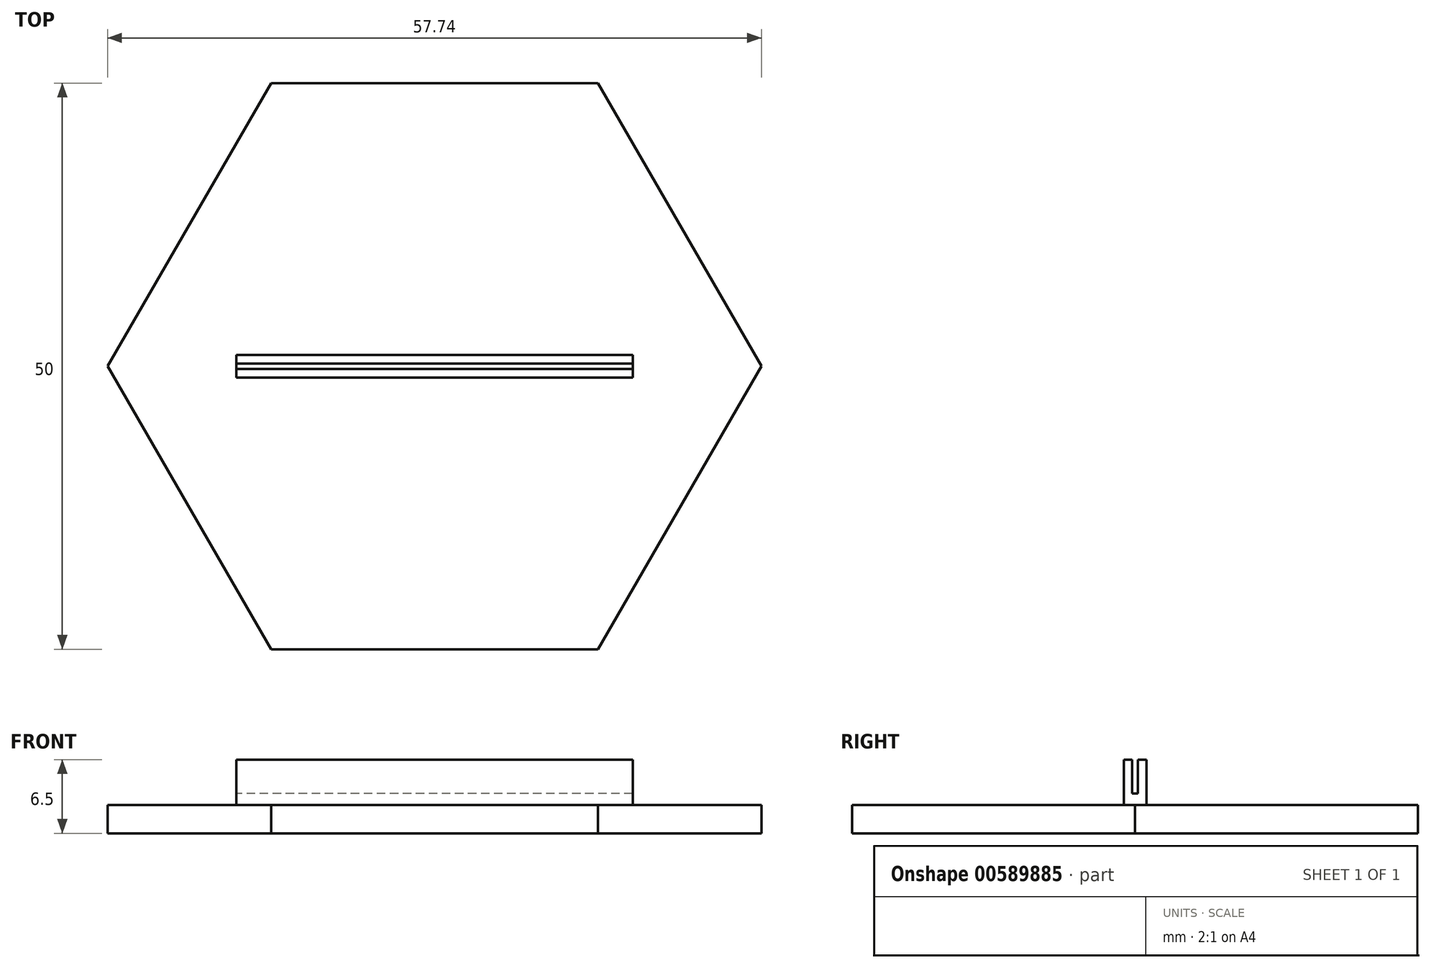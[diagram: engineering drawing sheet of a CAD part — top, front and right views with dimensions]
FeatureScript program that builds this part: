
annotation { "Feature Type Name" : "Feature", "Feature Type Description" : "" }
export const myFeature = defineFeature(function(context is Context, id is Id, definition is map)
    precondition{}
    {
        {
            var Q0;
            Q0=qCreatedBy(makeId("Top.planeOp"),FACE);
            var sketch = newSketch(context, id + "F0", { "sketchPlane" : qUnion([Q0])});
            skCircle(sketch, "E0.cCircle", {"center": v(0, 0) * mm, "radius": 25 * mm, "construction": true});
            skLineSegment(sketch, "E0.0", {"start": v(14.43, -25) * mm, "end": v(-14.43, -25) * mm});
            skLineSegment(sketch, "E0.1", {"start": v(-14.43, -25) * mm, "end": v(-28.87, 0) * mm});
            skLineSegment(sketch, "E0.2", {"start": v(-28.87, 0) * mm, "end": v(-14.43, 25) * mm});
            skLineSegment(sketch, "E0.3", {"start": v(-14.43, 25) * mm, "end": v(14.43, 25) * mm});
            skLineSegment(sketch, "E0.4", {"start": v(14.43, 25) * mm, "end": v(28.87, 0) * mm});
            skLineSegment(sketch, "E0.5", {"start": v(28.87, 0) * mm, "end": v(14.43, -25) * mm});
            skPoint(sketch, "E0.0.midPoint", {"position": v(0, -25) * mm});
            skSolve(sketch);
        }
        {
            var Q0;
            Q0 = qSketchRegion(id + "F0", true);
            extrude(context, id + "F1", {"entities" : qUnion([Q0]), "depth" : 2.5 * mm, "offsetDistance" : 25 * mm});
        }
        {
            var Q0;
            Q0=makeQuery(id+"F1.opExtrude","CAP_FACE",FACE,{"disambiguationData":[OSD([sQuery(id+"F0.wireOp",EDGE,"E0.0"),sQuery(id+"F0.wireOp",EDGE,"E0.1"),sQuery(id+"F0.wireOp",EDGE,"E0.2"),sQuery(id+"F0.wireOp",EDGE,"E0.3"),sQuery(id+"F0.wireOp",EDGE,"E0.4"),sQuery(id+"F0.wireOp",EDGE,"E0.5")])],"isStart":false});
            var sketch = newSketch(context, id + "F2", { "sketchPlane" : qUnion([Q0])});
            skLineSegment(sketch, "E1.bottom", {"start": v(17.5, -1) * mm, "end": v(-17.5, -1) * mm});
            skLineSegment(sketch, "E1.top", {"start": v(17.5, 1) * mm, "end": v(-17.5, 1) * mm});
            skLineSegment(sketch, "E1.left", {"start": v(17.5, -1) * mm, "end": v(17.5, 1) * mm});
            skLineSegment(sketch, "E1.right", {"start": v(-17.5, -1) * mm, "end": v(-17.5, 1) * mm});
            skPoint(sketch, "E1.middle", {"position": v(0, 0) * mm});
            skSolve(sketch);
        }
        {
            var Q0;
            Q0=makeQuery(id+"F2.imprint","IMPRINT",FACE,{"disambiguationData":[TD([[makeQuery(id+"F2.imprint","IMPRINT",EDGE,{"derivedFrom":sQuery(id+"F2.wireOp",EDGE,"E1.bottom")}),-1.0]])]});
            extrude(context, id + "F3", {"entities" : qUnion([Q0]), "operationType" : NewBodyOperationType.ADD, "depth" : 4 * mm, "offsetDistance" : 25 * mm});
        }
        {
            var Q0;
            Q0=makeQuery(id+"F3.opExtrude","CAP_FACE",FACE,{"disambiguationData":[OSD([sQuery(id+"F2.wireOp",EDGE,"E1.bottom"),sQuery(id+"F2.wireOp",EDGE,"E1.top"),sQuery(id+"F2.wireOp",EDGE,"E1.left"),sQuery(id+"F2.wireOp",EDGE,"E1.right")])],"isStart":false});
            var sketch = newSketch(context, id + "F4", { "sketchPlane" : qUnion([Q0])});
            skLineSegment(sketch, "E2.bottom", {"start": v(25.28, -0.25) * mm, "end": v(-24.72, -0.25) * mm});
            skLineSegment(sketch, "E2.top", {"start": v(25.28, 0.25) * mm, "end": v(-24.72, 0.25) * mm});
            skLineSegment(sketch, "E2.left", {"start": v(25.28, -0.25) * mm, "end": v(25.28, 0.25) * mm});
            skLineSegment(sketch, "E2.right", {"start": v(-24.72, -0.25) * mm, "end": v(-24.72, 0.25) * mm});
            skPoint(sketch, "E2.middle", {"position": v(0.28, 0) * mm});
            skSolve(sketch);
        }
        {
            var Q0;
            Q0 = qSketchRegion(id + "F4", true);
            extrude(context, id + "F5", {"entities" : qUnion([Q0]), "operationType" : NewBodyOperationType.REMOVE, "oppositeDirection" : true, "depth" : 3 * mm, "offsetDistance" : 25 * mm});
        }
    });
